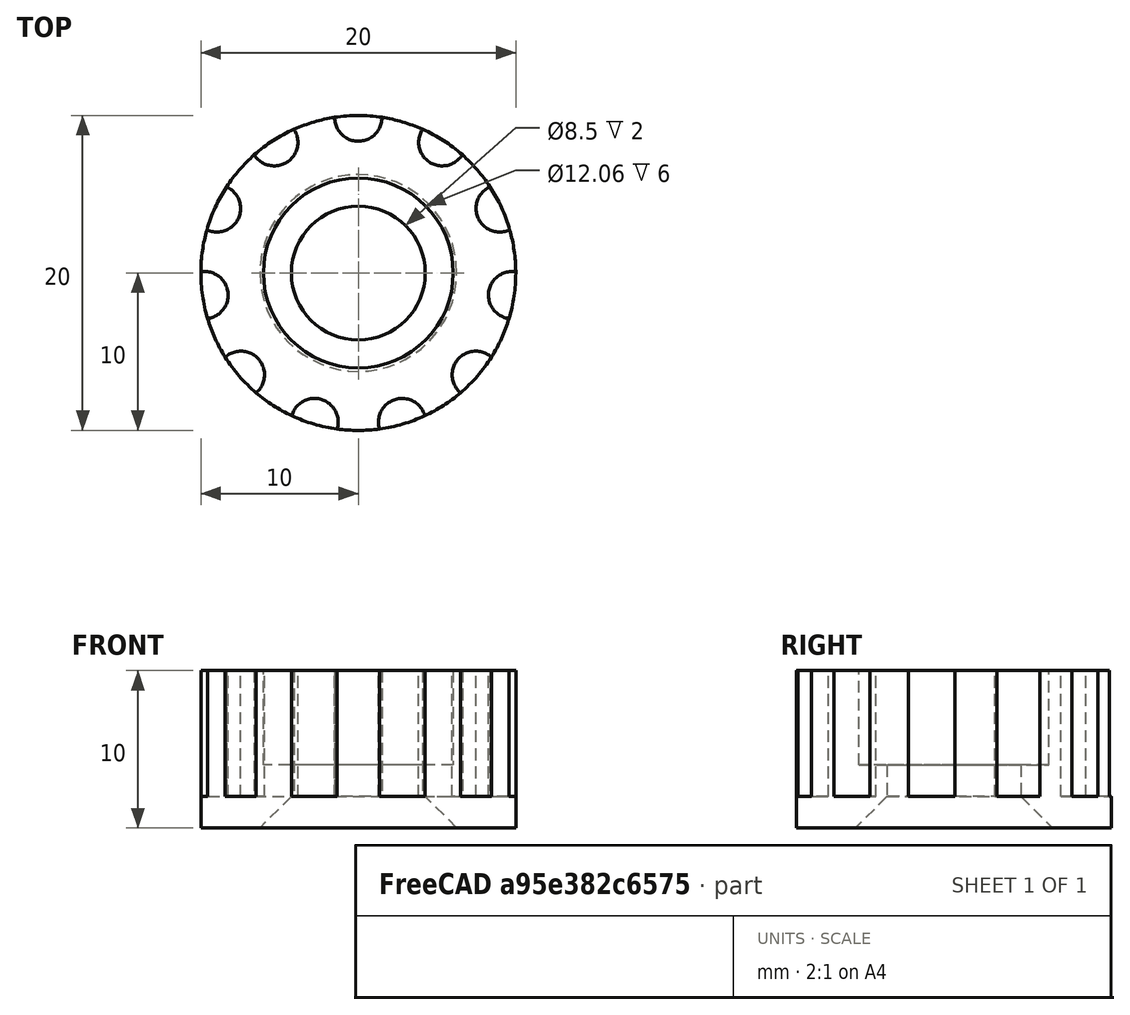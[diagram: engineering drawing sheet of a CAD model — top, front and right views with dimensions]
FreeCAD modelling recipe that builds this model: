
FCSTD DOCUMENT  (FreeCAD 0.19R)
Label: ValveStemFingerNut2
License: All rights reserved
LicenseURL: http://en.wikipedia.org/wiki/All_rights_reserved
objects: Sketcher::SketchObject×4, PartDesign::Pocket×3, PartDesign::Pad×1, PartDesign::PolarPattern×1, PartDesign::Chamfer×1, PartDesign::Body×1, Mesh::Feature×1
note: 16 computed .brp shape members not serialized (recipe doc carries the construction recipe); baked Part::Feature solids carry a one-line shape summary decoded from their .brp

FEATURE [Sketcher::SketchObject] Sketch
  FullyConstrained = true
  MapMode = 5
  Support = -> [XY_Plane]
  sketch-geometry (1):
    g0: Circle CenterX=0 CenterY=0 CenterZ=0 NormalX=0 NormalY=0 NormalZ=1 AngleXU=0 Radius=10
  constraints (2):
    c: Coincident(g0,g-1)
    c: Radius(g0) = 10
FEATURE [PartDesign::Pad] Pad
  Direction = (1,1,1)
  Length = 10
  Length2 = 100
  Profile = -> Sketch
  Type = 0
FEATURE [Sketcher::SketchObject] Sketch001
  FullyConstrained = true
  MapMode = 5
  Placement = pos=(0,0,10) rot=(0,0,1;0rad)
  Support = -> [Pad]
  sketch-geometry (1):
    g0: Circle CenterX=0 CenterY=0 CenterZ=0 NormalX=0 NormalY=0 NormalZ=1 AngleXU=0 Radius=6.03
  constraints (2):
    c: Coincident(g0,g-1)
    c: Radius(g0) = 6.03
FEATURE [PartDesign::Pocket] Pocket
  BaseFeature = -> Pad
  Length = 6
  Length2 = 100
  Profile = -> Sketch001
  Type = 0
FEATURE [Sketcher::SketchObject] Sketch002
  FullyConstrained = true
  MapMode = 5
  Placement = pos=(0,0,0) rot=(1,0,0;3.14159rad)
  Support = -> [Pocket]
  sketch-geometry (1):
    g0: Circle CenterX=0 CenterY=0 CenterZ=0 NormalX=0 NormalY=0 NormalZ=1 AngleXU=0 Radius=4.25
  constraints (2):
    c: Coincident(g0,g-1)
    c: Radius(g0) = 4.25
FEATURE [PartDesign::Pocket] Pocket001
  BaseFeature = -> Pocket
  Length = 5
  Length2 = 100
  Profile = -> Sketch002
  Type = 0
FEATURE [Sketcher::SketchObject] Sketch003
  FullyConstrained = false
  MapMode = 5
  Placement = pos=(0,0,10) rot=(0,0,1;0rad)
  Support = -> [Pocket001]
  sketch-geometry (1):
    g0: Circle CenterX=0 CenterY=9.86833 CenterZ=0 NormalX=0 NormalY=0 NormalZ=1 AngleXU=0 Radius=1.5
  constraints (2):
    c: PointOnObject(g0,g-2)
    c: Radius(g0) = 1.5
FEATURE [PartDesign::Pocket] Pocket002
  BaseFeature = -> Pocket001
  Length = 8
  Length2 = 100
  Profile = -> Sketch003
  Type = 0
FEATURE [PartDesign::PolarPattern] PolarPattern
  Angle = 360
  Axis = -> Sketch003 [N_Axis]
  BaseFeature = -> Pocket002
  Occurrences = 11
  Originals = -> [Pocket002]
FEATURE [PartDesign::Chamfer] Chamfer
  Angle = 45
  Base = -> PolarPattern [Edge48]
  BaseFeature = -> PolarPattern
  ChamferType = 0
  FlipDirection = false
  Size = 2
  Size2 = 1
  SupportTransform = false
FEATURE [PartDesign::Body] Body
  Group = -> [Sketch,Pad,Sketch001,Pocket,Sketch002,Pocket001,Sketch003,Pocket002,PolarPattern,Chamfer]
  Origin = -> Origin
  Tip = -> Chamfer
FEATURE [Mesh::Feature] Mesh  label="Chamfer (Meshed)"
